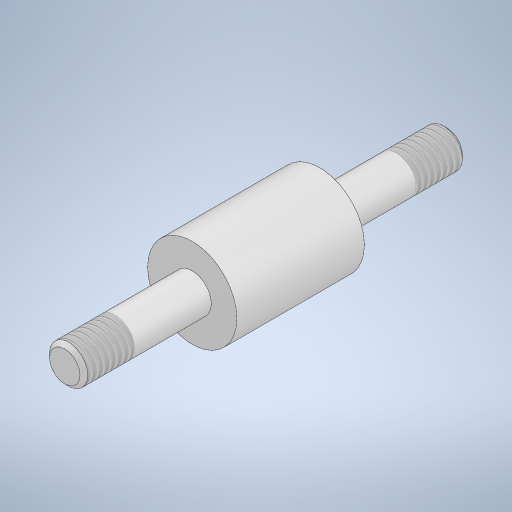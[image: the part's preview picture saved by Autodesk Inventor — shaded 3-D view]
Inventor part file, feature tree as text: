
AUTODESK INVENTOR PART (.ipt)
format: ipt  version: 2024.3 (Build 283343000, 343)  size: 267,776 bytes
history: native  units: mm
features: thread x2, other x1, revolve x1, chamfer x1, sketch x1
ambient origin geometry x8: Origin, YZ Plane, XZ Plane, XY Plane, X Axis, Y Axis, Z Axis, Center Point
bodies: Body1 (feature_tree)
feature tree (6):
  other  "Sólido1"
  revolve  "Revolución1"  [1 undecoded]
  thread  "Rosca2"  [1 undecoded]
  thread  "Rosca3"  [1 undecoded]
  chamfer  "Chaflán1"  Distance=4.0mm
  sketch  "Boceto1"  dims[d0=7.0mm d1=3.0mm d3=30.0mm d4=90.0deg d7=4.0mm d8=0.0mm d9=4.0mm d10=6.0mm d11=0.306725mm d12=2.0mm d13=45.0deg]
note: 3 required parameter values undecoded (feature->parameter linkage not recoverable at this tier; creation-order binding heuristic only, values carry confidence <= 0.55)